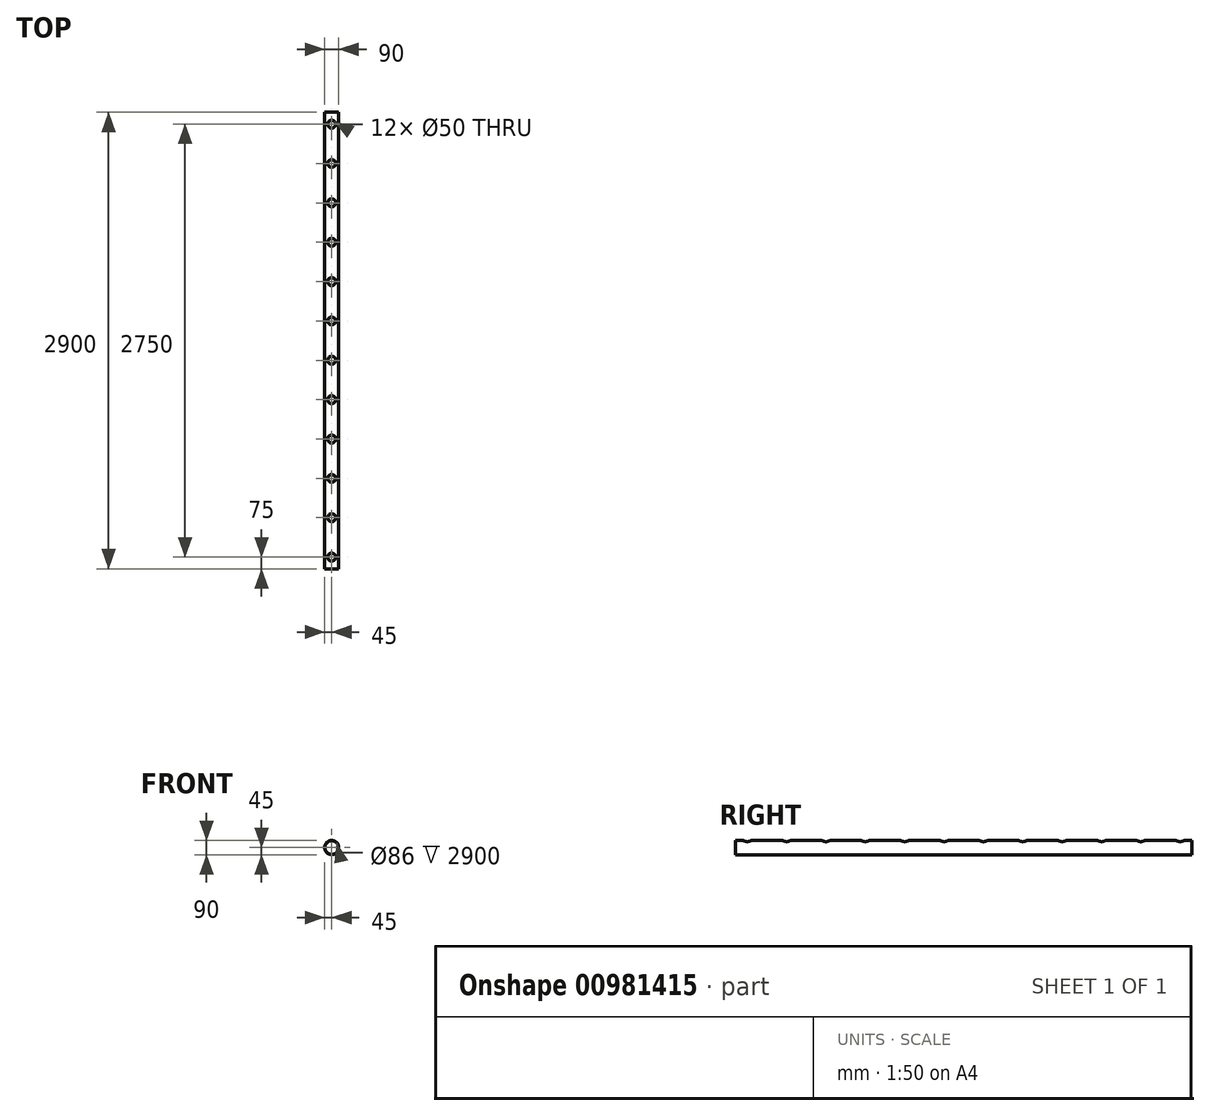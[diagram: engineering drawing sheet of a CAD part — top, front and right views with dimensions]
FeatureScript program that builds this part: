
annotation { "Feature Type Name" : "Feature", "Feature Type Description" : "" }
export const myFeature = defineFeature(function(context is Context, id is Id, definition is map)
    precondition{}
    {
        {
            var Q0;
            Q0=qCreatedBy(makeId("Front.planeOp"),FACE);
            var sketch = newSketch(context, id + "F0", { "sketchPlane" : qUnion([Q0])});
            skCircle(sketch, "E0", {"center": v(0, 0) * mm, "radius": 45 * mm});
            skCircle(sketch, "E1.0", {"center": v(0, 0) * mm, "radius": 43 * mm});
            skSolve(sketch);
        }
        {
            var Q0;
            Q0=qSketchRegion(id+"F0",true);
            extrude(context, id + "F1", {"entities" : qUnion([Q0]), "endBound" : BoundingType.SYMMETRIC, "depth" : 2900 * mm, "offsetDistance" : 25 * mm});
        }
        {
            var Q0;
            Q0=qCreatedBy(makeId("Top.planeOp"),FACE);
            cPlane(context, id + "F2", {"entities" : qUnion([Q0]), "cplaneType" : CPlaneType.OFFSET, "offset" : 45 * mm, "width" : 150 * mm, "height" : 150 * mm});
        }
        {
            var Q0;
            Q0=qCreatedBy(id+"F2.planeOp",FACE);
            var sketch = newSketch(context, id + "F3", { "sketchPlane" : qUnion([Q0])});
            skPoint(sketch, "E2", {"position": v(0, -1375) * mm});
            skPoint(sketch, "E3", {"position": v(0, -1125) * mm});
            skPoint(sketch, "E4", {"position": v(0, -875) * mm});
            skPoint(sketch, "E5", {"position": v(0, -625) * mm});
            skPoint(sketch, "E6", {"position": v(0, -375) * mm});
            skPoint(sketch, "E7", {"position": v(0, -125) * mm});
            skPoint(sketch, "E8", {"position": v(0, 125) * mm});
            skPoint(sketch, "E9", {"position": v(0, 375) * mm});
            skPoint(sketch, "E10", {"position": v(0, 625) * mm});
            skPoint(sketch, "E11", {"position": v(0, 875) * mm});
            skPoint(sketch, "E12", {"position": v(0, 1125) * mm});
            skPoint(sketch, "E13", {"position": v(0, 1375) * mm});
            skSolve(sketch);
        }
        {
            var Q0;
            Q0=sQuery(id+"F3.wireOp",VERTEX,"E2");
            var Q1;
            Q1=sQuery(id+"F3.wireOp",VERTEX,"E3");
            var Q2;
            Q2=sQuery(id+"F3.wireOp",VERTEX,"E4");
            var Q3;
            Q3=sQuery(id+"F3.wireOp",VERTEX,"E5");
            var Q4;
            Q4=sQuery(id+"F3.wireOp",VERTEX,"E6");
            var Q5;
            Q5=sQuery(id+"F3.wireOp",VERTEX,"E7");
            var Q6;
            Q6=sQuery(id+"F3.wireOp",VERTEX,"E8");
            var Q7;
            Q7=sQuery(id+"F3.wireOp",VERTEX,"E9");
            var Q8;
            Q8=sQuery(id+"F3.wireOp",VERTEX,"E10");
            var Q9;
            Q9=sQuery(id+"F3.wireOp",VERTEX,"E11");
            var Q10;
            Q10=sQuery(id+"F3.wireOp",VERTEX,"E12");
            var Q11;
            Q11=sQuery(id+"F3.wireOp",VERTEX,"E13");
            var Q12;
            Q12=sQuery(id+"F3.wireOp",VERTEX,"d6d3cdd6-09bc-4208-8bfb-94afde8f0a46");
            var Q13;
            Q13=sQuery(id+"F3.wireOp",VERTEX,"734153c6-2249-4abd-a6b6-f48a35ac855c");
            var Q14;
            Q14=sQuery(id+"F3.wireOp",VERTEX,"46e0f81d-7a3e-4eb5-89d9-9d338da62cf5");
            var Q15;
            Q15=sQuery(id+"F3.wireOp",VERTEX,"f4cd902c-7ee6-44a1-aa6d-15636b985a91");
            var Q16;
            Q16=sQuery(id+"F3.wireOp",VERTEX,"a0becd45-3f8c-473a-b9c5-eca89ffffb86");
            var Q17;
            Q17=sQuery(id+"F3.wireOp",VERTEX,"449d03d7-6090-459a-adaf-9611daa20e82");
            var Q18;
            Q18=sQuery(id+"F3.wireOp",VERTEX,"1d2369e2-f7b6-45cb-9ac7-ef4d2139859a");
            var Q19;
            Q19=sQuery(id+"F3.wireOp",VERTEX,"4217ffee-23aa-4e57-b56b-1031955cdd20");
            var Q20;
            Q20=sQuery(id+"F3.wireOp",VERTEX,"f9e667d2-43f0-46cb-85dd-7700daad2ab1");
            var Q21;
            Q21=sQuery(id+"F3.wireOp",VERTEX,"a141cc4f-d6fa-4136-a428-d91cc8b08e23");
            var Q22;
            Q22=sQuery(id+"F3.wireOp",VERTEX,"6950c5e6-caf7-4953-8c5b-56709a9cffe9");
            var Q23;
            Q23=sQuery(id+"F3.wireOp",VERTEX,"1581daf2-9304-4365-a3cc-e960652a3bf4");
            var Q24;
            Q24=sQuery(id+"F3.wireOp",VERTEX,"25a0b738-50ad-46bb-ba52-db4eb22869ea");
            var Q25;
            Q25=sQuery(id+"F3.wireOp",VERTEX,"23c6b068-1da5-4682-a93c-07f6e733a235");
            var Q26;
            Q26=sQuery(id+"F3.wireOp",VERTEX,"77491461-51bd-4097-a69a-b50156a0fef7");
            var Q27;
            Q27=sQuery(id+"F3.wireOp",VERTEX,"89e2eaf9-af87-4198-a739-5b01357332c3");
            var Q28;
            Q28=sQuery(id+"F3.wireOp",VERTEX,"a31ac070-19d1-4092-b391-6f630edb761b");
            var Q29;
            Q29=makeQuery(id+"F1.opExtrude","SWEPT_BODY",BODY,{"disambiguationData":[OSD([sQuery(id+"F0.wireOp",EDGE,"E0"),sQuery(id+"F0.wireOp",EDGE,"E1.0")])]});
            hole(context, id + "F4", {"style" : HoleStyle.SIMPLE, "endStyle" : HoleEndStyle.BLIND, "holeDiameter" : 50 * mm, "majorDiameter" : 5 * mm, "holeDepth" : 50 * mm, "isTappedThrough" : true, "tappedDepth" : 12 * mm, "tapClearance" : 3, "startFromSketch" : true, "locations" : qUnion([Q0, Q1, Q2, Q3, Q4, Q5, Q6, Q7, Q8, Q9, Q10, Q11, Q12, Q13, Q14, Q15, Q16, Q17, Q18, Q19, Q20, Q21, Q22, Q23, Q24, Q25, Q26, Q27, Q28]), "scope" : qUnion([Q29])});
        }
    });
